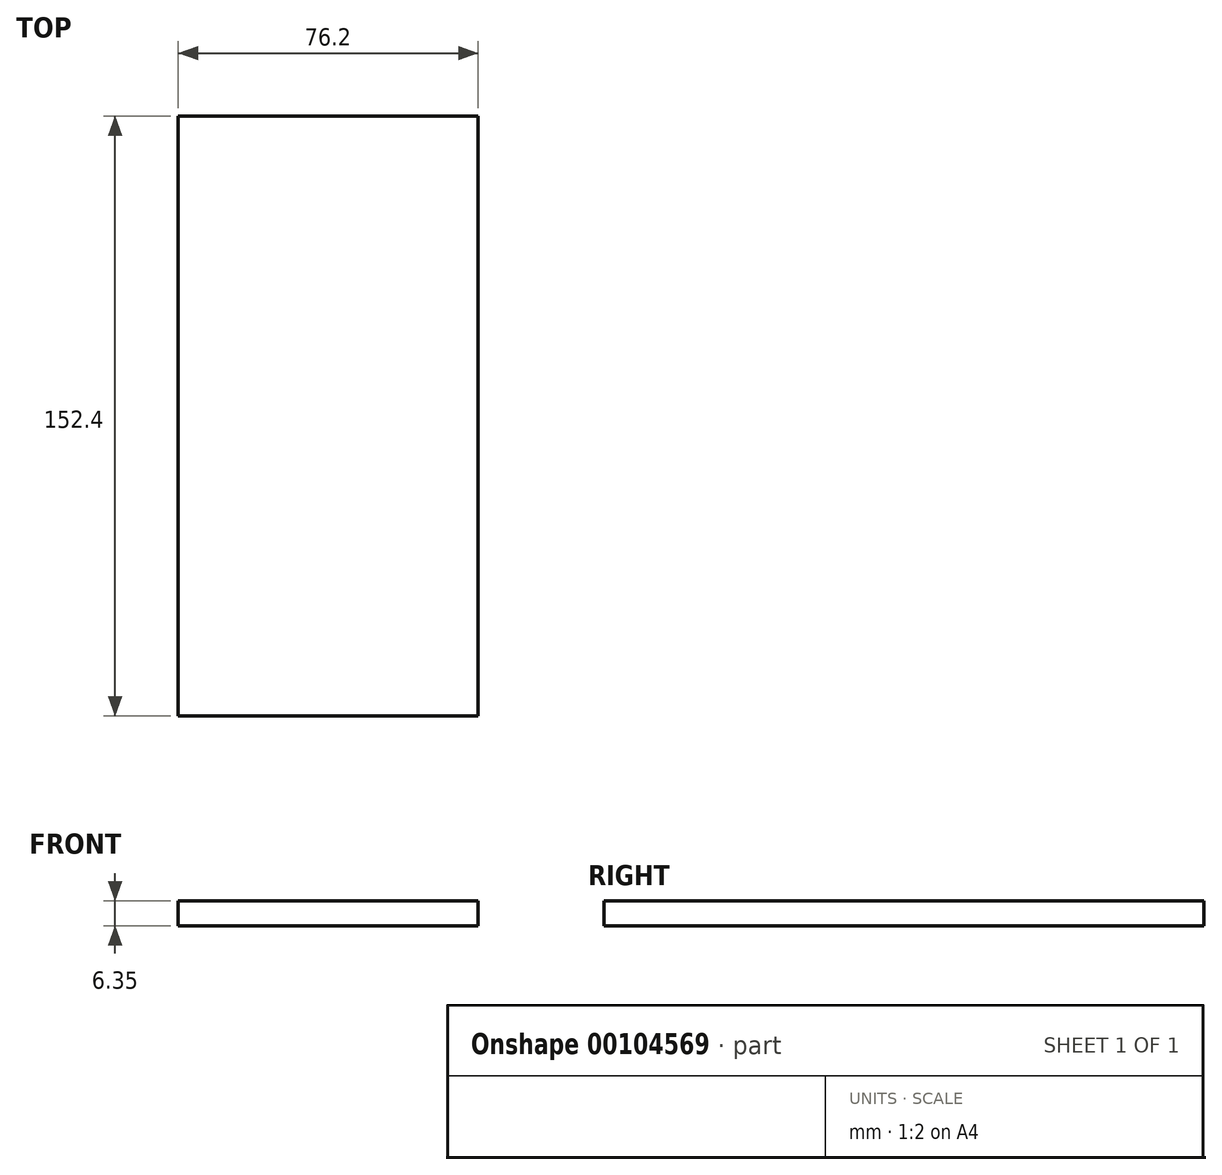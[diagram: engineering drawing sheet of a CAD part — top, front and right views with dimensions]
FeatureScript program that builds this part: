
annotation { "Feature Type Name" : "Feature", "Feature Type Description" : "" }
export const myFeature = defineFeature(function(context is Context, id is Id, definition is map)
    precondition{}
    {
        {
            var Q0;
            Q0=qCreatedBy(makeId("Top.planeOp"),FACE);
            var sketch = newSketch(context, id + "F0", { "sketchPlane" : qUnion([Q0])});
            skLineSegment(sketch, "E0.bottom", {"start": v(-88.39, 91.04) * mm, "end": v(-12.19, 91.04) * mm});
            skLineSegment(sketch, "E0.top", {"start": v(-88.39, -61.36) * mm, "end": v(-12.19, -61.36) * mm});
            skLineSegment(sketch, "E0.left", {"start": v(-88.39, 91.04) * mm, "end": v(-88.39, -61.36) * mm});
            skLineSegment(sketch, "E0.right", {"start": v(-12.19, 91.04) * mm, "end": v(-12.19, -61.36) * mm});
            skSolve(sketch);
        }
        {
            var Q0;
            Q0=makeQuery(id+"F0.imprint","IMPRINT",FACE,{"disambiguationData":[TD([[makeQuery(id+"F0.imprint","IMPRINT",EDGE,{"derivedFrom":sQuery(id+"F0.wireOp",EDGE,"E0.bottom")}),-1.0]])]});
            extrude(context, id + "F1", {"entities" : qUnion([Q0]), "depth" : 6.35 * mm});
        }
    });
